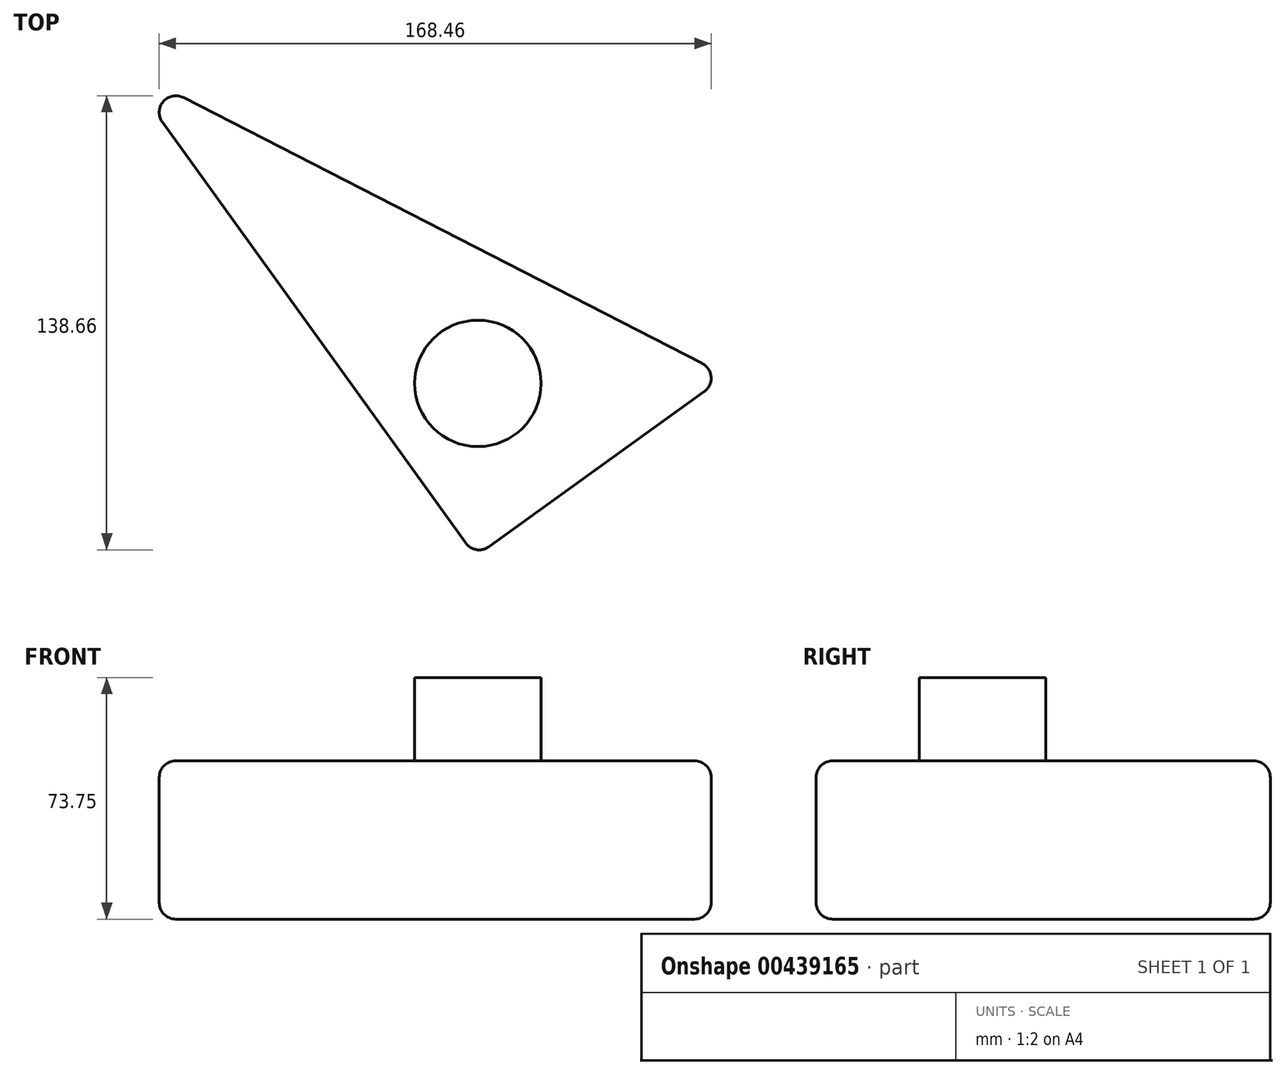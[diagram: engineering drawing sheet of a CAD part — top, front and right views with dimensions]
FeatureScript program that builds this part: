
annotation { "Feature Type Name" : "Feature", "Feature Type Description" : "" }
export const myFeature = defineFeature(function(context is Context, id is Id, definition is map)
    precondition{}
    {
        {
            var Q0;
            Q0=qCreatedBy(makeId("Top.planeOp"),FACE);
            var sketch = newSketch(context, id + "F0", { "sketchPlane" : qUnion([Q0])});
            skLineSegment(sketch, "E0", {"start": v(-77.26, 73.9) * mm, "end": v(30.61, -75.83) * mm});
            skLineSegment(sketch, "E1", {"start": v(30.61, -75.83) * mm, "end": v(107.2, -20.65) * mm});
            skLineSegment(sketch, "E2", {"start": v(107.2, -20.65) * mm, "end": v(-77.26, 73.9) * mm});
            skSolve(sketch);
        }
        {
            var Q0;
            Q0 = qSketchRegion(id + "F0", true);
            extrude(context, id + "F1", {"entities" : qUnion([Q0]), "depth" : 48.35 * mm});
        }
        {
            var Q0;
            Q0=makeQuery(id+"F1.opExtrude","SWEPT_EDGE",EDGE,{"disambiguationData":[OSD([sQuery(id+"F0.wireOp",EDGE,"E0"),sQuery(id+"F0.wireOp",EDGE,"E2")])]});
            var Q1;
            Q1=makeQuery(id+"F1.opExtrude","CAP_EDGE",EDGE,{"disambiguationData":[OSD([sQuery(id+"F0.wireOp",EDGE,"E1")])],"isStart":false});
            var Q2;
            Q2=makeQuery(id+"F1.opExtrude","SWEPT_EDGE",EDGE,{"disambiguationData":[OSD([sQuery(id+"F0.wireOp",EDGE,"E1"),sQuery(id+"F0.wireOp",EDGE,"E2")])]});
            var Q3;
            Q3=makeQuery(id+"F1.opExtrude","CAP_EDGE",EDGE,{"disambiguationData":[OSD([sQuery(id+"F0.wireOp",EDGE,"E2")])],"isStart":true});
            var Q4;
            Q4=makeQuery(id+"F1.opExtrude","CAP_EDGE",EDGE,{"disambiguationData":[OSD([sQuery(id+"F0.wireOp",EDGE,"E2")])],"isStart":false});
            var Q5;
            Q5=makeQuery(id+"F1.opExtrude","CAP_EDGE",EDGE,{"disambiguationData":[OSD([sQuery(id+"F0.wireOp",EDGE,"E0")])],"isStart":true});
            var Q6;
            Q6=makeQuery(id+"F1.opExtrude","CAP_EDGE",EDGE,{"disambiguationData":[OSD([sQuery(id+"F0.wireOp",EDGE,"E1")])],"isStart":true});
            var Q7;
            Q7=makeQuery(id+"F1.opExtrude","SWEPT_EDGE",EDGE,{"disambiguationData":[OSD([sQuery(id+"F0.wireOp",EDGE,"E0"),sQuery(id+"F0.wireOp",EDGE,"E1")])]});
            var Q8;
            Q8=makeQuery(id+"F1.opExtrude","CAP_EDGE",EDGE,{"disambiguationData":[OSD([sQuery(id+"F0.wireOp",EDGE,"E0")])],"isStart":false});
            fillet(context, id + "F2", {"entities" : qUnion([Q0, Q1, Q2, Q3, Q4, Q5, Q6, Q7, Q8]), "radius" : 5.08 * mm, "tangentPropagation" : true, "allowEdgeOverflow" : false});
        }
        {
            var Q0;
            Q0=makeQuery(id+"F1.opExtrude","CAP_FACE",FACE,{"disambiguationData":[OSD([sQuery(id+"F0.wireOp",EDGE,"E0"),sQuery(id+"F0.wireOp",EDGE,"E1"),sQuery(id+"F0.wireOp",EDGE,"E2")])],"isStart":false});
            var sketch = newSketch(context, id + "F3", { "sketchPlane" : qUnion([Q0])});
            skCircle(sketch, "E3", {"center": v(0, 6.44) * mm, "radius": 1.1 * mm});
            skCircle(sketch, "E4", {"center": v(13.08, 21.88) * mm, "radius": 20.24 * mm});
            skCircle(sketch, "E5", {"center": v(31.38, -22.98) * mm, "radius": 19.3 * mm});
            skCircle(sketch, "E6", {"center": v(5.04, 21.7) * mm, "radius": 21.41 * mm});
            skSolve(sketch);
        }
        {
            var Q0;
            Q0=makeQuery(id+"F3.imprint","IMPRINT",FACE,{"disambiguationData":[TD([[makeQuery(id+"F3.imprint","IMPRINT",EDGE,{"derivedFrom":sQuery(id+"F3.wireOp",EDGE,"E5")}),1.0]])]});
            var sketch = newSketch(context, id + "F4", { "sketchPlane" : qUnion([Q0])});
            skSolve(sketch);
        }
        {
            var Q0;
            Q0 = qSketchRegion(id + "F4", true);
            var Q1;
            Q1=makeQuery(id+"F4.imprint","IMPRINT",FACE,{"disambiguationData":[TD([[makeQuery(id+"F4.imprint","IMPRINT",EDGE,{"derivedFrom":makeQuery(id+"F3.imprint","IMPRINT",EDGE,{"derivedFrom":sQuery(id+"F3.wireOp",EDGE,"E5")})}),1.0]])]});
            extrude(context, id + "F5", {"entities" : qUnion([Q0, Q1]), "operationType" : NewBodyOperationType.ADD, "depth" : 25.4 * mm});
        }
    });
